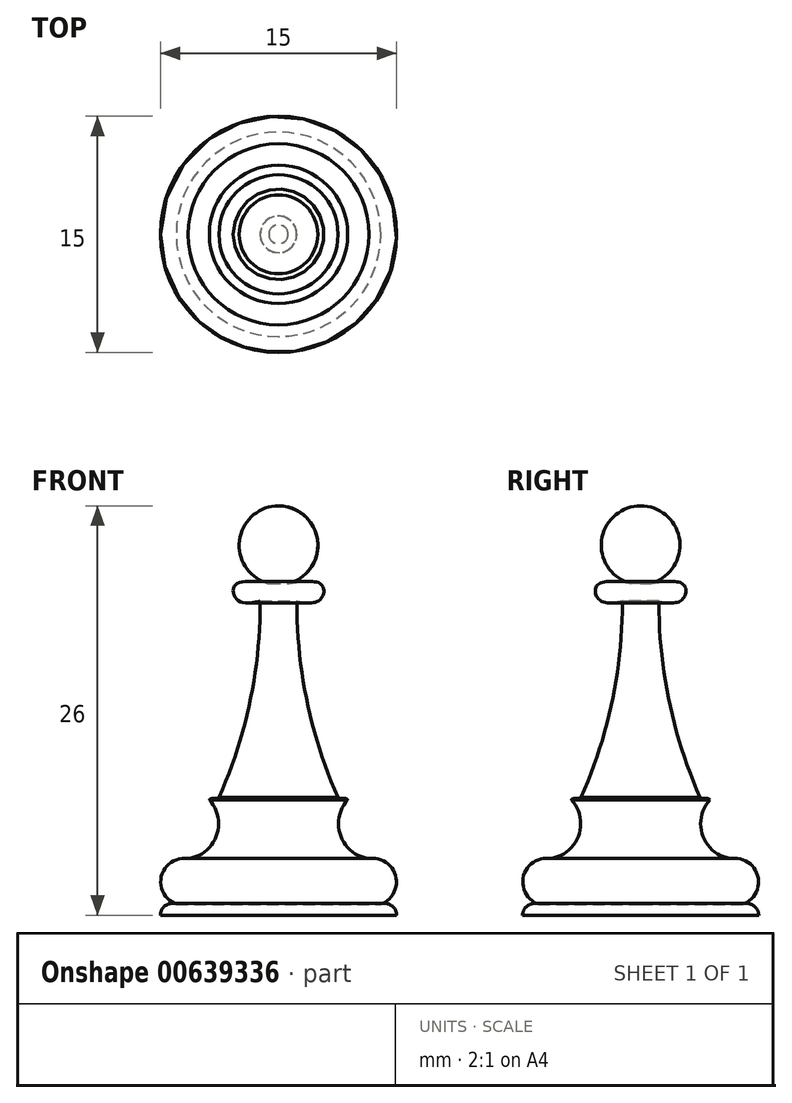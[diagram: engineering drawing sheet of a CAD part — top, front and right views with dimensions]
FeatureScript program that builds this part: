
annotation { "Feature Type Name" : "Feature", "Feature Type Description" : "" }
export const myFeature = defineFeature(function(context is Context, id is Id, definition is map)
    precondition{}
    {
        {
            var Q0;
            Q0=qCreatedBy(makeId("Front.planeOp"),FACE);
            var sketch = newSketch(context, id + "F0", { "sketchPlane" : qUnion([Q0])});
            skLineSegment(sketch, "E0", {"start": v(0, 0) * mm, "end": v(7.5, 0) * mm});
            skLineSegment(sketch, "E1", {"start": v(0, 0) * mm, "end": v(0, 26) * mm});
            skArc(sketch, "E2", {"start": v(7.5, 0) * mm, "mid": v(7.18, 0.61) * mm, "end": v(6.5, 0.7) * mm});
            skArc(sketch, "E3", {"start": v(6.5, 0.7) * mm, "mid": v(7.44, 2.49) * mm, "end": v(5.75, 3.6) * mm});
            skArc(sketch, "E4", {"start": v(0.61, 21.08) * mm, "mid": v(2.48, 23.8) * mm, "end": v(0, 26) * mm});
            skFitSpline(sketch, "E5", {"points": [v(1.17, 19.95) * mm, v(2.51, 19.95) * mm, v(2.7, 21.02) * mm, v(0.61, 21.08) * mm], "startDerivative": vector(1.5, -0.33) * mm, "endDerivative": vector(-3.23, -0.34) * mm});
            skArc(sketch, "E6", {"start": v(4.4, 7.32) * mm, "mid": v(3.95, 5.05) * mm, "end": v(5.75, 3.6) * mm});
            skArc(sketch, "E7", {"start": v(1.17, 19.95) * mm, "mid": v(1.81, 13.58) * mm, "end": v(3.78, 7.48) * mm});
            skFitSpline(sketch, "E8", {"points": [v(4.4, 7.32) * mm, v(4.36, 7.37) * mm, v(4.26, 7.41) * mm, v(4.01, 7.43) * mm, v(3.85, 7.37) * mm, v(3.78, 7.48) * mm], "startDerivative": vector(-0.2, 0.42) * mm, "endDerivative": vector(-0.27, 0.78) * mm});
            skSolve(sketch);
        }
        {
            var Q0;
            Q0=makeQuery(id+"F0.imprint","IMPRINT",FACE,{"disambiguationData":[TD([[makeQuery(id+"F0.imprint","IMPRINT",EDGE,{"derivedFrom":sQuery(id+"F0.wireOp",EDGE,"E0")}),1.0]])]});
            var Q1;
            Q1=sQuery(id+"F0.wireOp",EDGE,"E1");
            revolve(context, id + "F1", {"entities" : qUnion([Q0]), "axis" : qUnion([Q1]), "revolveType" : RevolveType.FULL});
        }
    });
